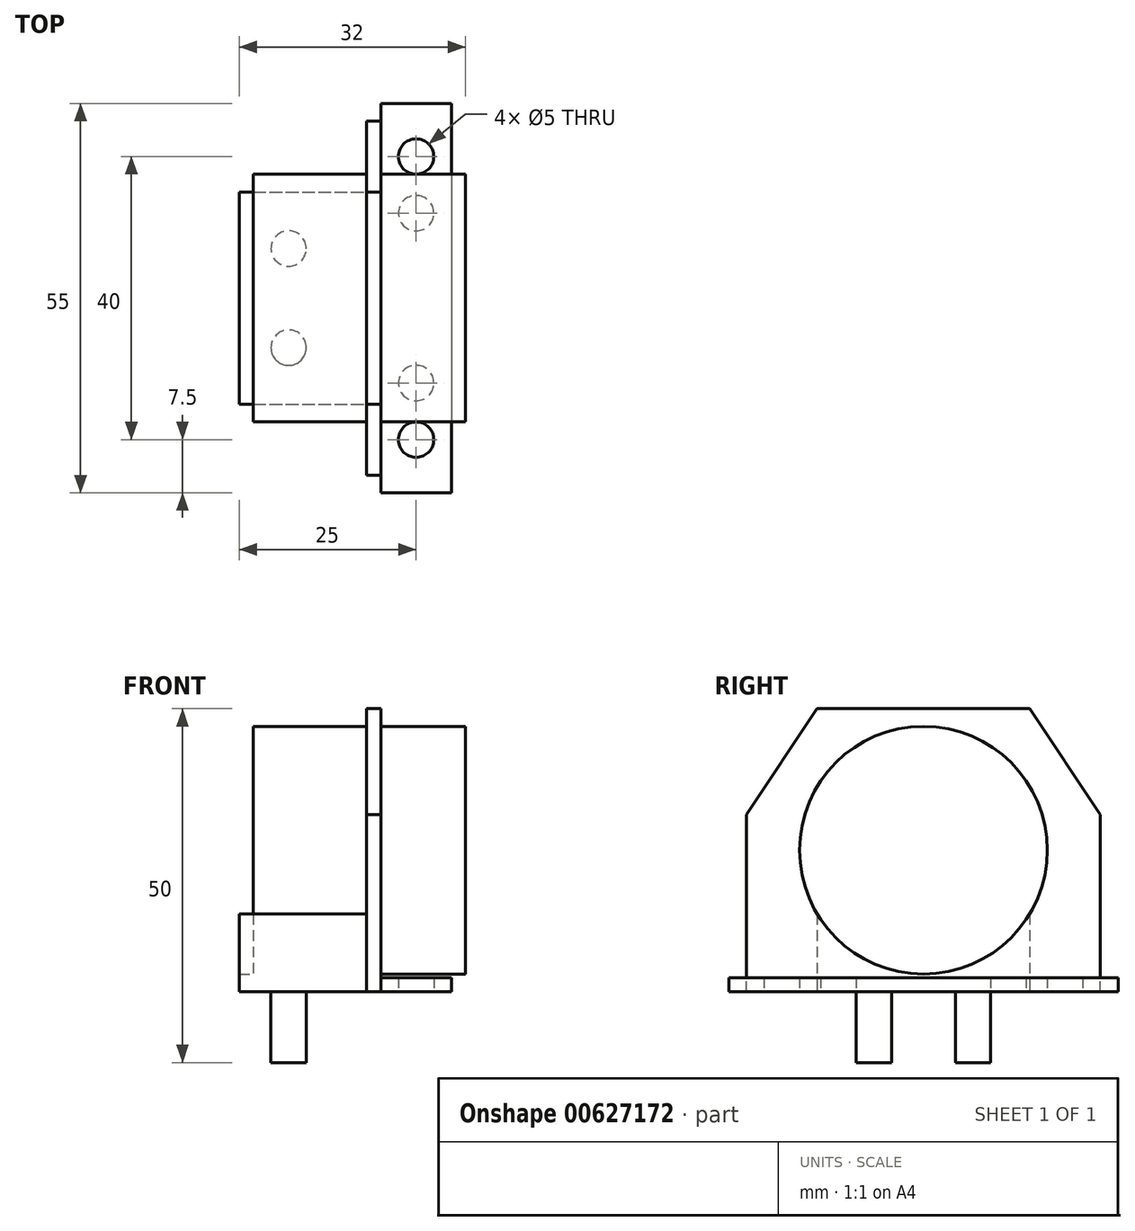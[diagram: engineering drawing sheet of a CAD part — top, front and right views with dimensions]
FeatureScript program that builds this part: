
annotation { "Feature Type Name" : "Feature", "Feature Type Description" : "" }
export const myFeature = defineFeature(function(context is Context, id is Id, definition is map)
    precondition{}
    {
        {
            var Q0;
            Q0=qCreatedBy(makeId("Top.planeOp"),FACE);
            var sketch = newSketch(context, id + "F0", { "sketchPlane" : qUnion([Q0])});
            skLineSegment(sketch, "E0.bottom", {"start": v(5, 27.5) * mm, "end": v(-5, 27.5) * mm});
            skLineSegment(sketch, "E0.top", {"start": v(5, -27.5) * mm, "end": v(-5, -27.5) * mm});
            skLineSegment(sketch, "E0.left", {"start": v(5, 27.5) * mm, "end": v(5, -27.5) * mm});
            skLineSegment(sketch, "E0.right", {"start": v(-5, 27.5) * mm, "end": v(-5, -27.5) * mm});
            skPoint(sketch, "E0.middle", {"position": v(0, 0) * mm});
            skCircle(sketch, "E1", {"center": v(0, 20) * mm, "radius": 2.5 * mm});
            skCircle(sketch, "E2", {"center": v(0, 12) * mm, "radius": 2.5 * mm});
            skCircle(sketch, "E3.MirrorC", {"center": v(0, -12) * mm, "radius": 2.5 * mm});
            skCircle(sketch, "E4.MirrorC", {"center": v(0, -20) * mm, "radius": 2.5 * mm});
            skSolve(sketch);
        }
        {
            var Q0;
            Q0 = qSketchRegion(id + "F0", true);
            extrude(context, id + "F1", {"entities" : qUnion([Q0]), "depth" : 2 * mm, "offsetDistance" : 25 * mm});
        }
        {
            var Q0;
            Q0=makeQuery(id+"F1.opExtrude","SWEPT_FACE",FACE,{"disambiguationData":[OSD([sQuery(id+"F0.wireOp",EDGE,"E0.right")])]});
            var sketch = newSketch(context, id + "F2", { "sketchPlane" : qUnion([Q0])});
            skLineSegment(sketch, "E5", {"start": v(-25, 0) * mm, "end": v(-25, 25) * mm});
            skLineSegment(sketch, "E6", {"start": v(-15, 0) * mm, "end": v(-15, 40) * mm});
            skLineSegment(sketch, "E7", {"start": v(-25, 25) * mm, "end": v(-15, 40) * mm});
            skLineSegment(sketch, "E8", {"start": v(0, 40) * mm, "end": v(-15, 40) * mm});
            skLineSegment(sketch, "E9.MirrorCS", {"start": v(0, 40) * mm, "end": v(15, 40) * mm});
            skLineSegment(sketch, "E10.MirrorCS", {"start": v(15, 0) * mm, "end": v(15, 40) * mm});
            skLineSegment(sketch, "E11.MirrorCS", {"start": v(25, 25) * mm, "end": v(15, 40) * mm});
            skLineSegment(sketch, "E12.MirrorCS", {"start": v(25, 0) * mm, "end": v(25, 25) * mm});
            skCircle(sketch, "E13", {"center": v(0, 20) * mm, "radius": 17.5 * mm});
            skSolve(sketch);
        }
        {
            var Q0;
            {var subQ0=sQuery(id+"F2.wireOp",EDGE,"E6");var subQ1=sQuery(id+"F0.wireOp",EDGE,"E0.right");var subQ2=makeQuery(id+"F1.opExtrude","CAP_EDGE",EDGE,{"disambiguationData":[OSD([subQ1])],"isStart":true});var subQ3=makeQuery(id+"F2.imprint","INTERSECT",VERTEX,{"derivedFrom":[subQ2,subQ0]});Q0=makeQuery(id+"F2.imprint","IMPRINT",FACE,{"disambiguationData":[TD([[makeQuery(id+"F2.imprint","IMPRINT",EDGE,{"disambiguationData":[TD([[subQ3,-1.0]])],"derivedFrom":subQ0}),-1.0]])]});}
            var Q1;
            {var subQ0=sQuery(id+"F2.wireOp",EDGE,"E5");var subQ1=sQuery(id+"F0.wireOp",EDGE,"E0.right");var subQ2=makeQuery(id+"F1.opExtrude","CAP_EDGE",EDGE,{"disambiguationData":[OSD([subQ1])],"isStart":true});var subQ3=makeQuery(id+"F2.imprint","INTERSECT",VERTEX,{"derivedFrom":[subQ2,subQ0]});Q1=makeQuery(id+"F2.imprint","IMPRINT",FACE,{"disambiguationData":[TD([[makeQuery(id+"F2.imprint","IMPRINT",EDGE,{"disambiguationData":[TD([[subQ3,-1.0]])],"derivedFrom":subQ0}),-1.0]])]});}
            var Q2;
            {var subQ0=sQuery(id+"F2.wireOp",EDGE,"E10.MirrorCS");var subQ1=sQuery(id+"F0.wireOp",EDGE,"E0.right");var subQ2=makeQuery(id+"F1.opExtrude","CAP_EDGE",EDGE,{"disambiguationData":[OSD([subQ1])],"isStart":true});var subQ3=makeQuery(id+"F2.imprint","INTERSECT",VERTEX,{"derivedFrom":[subQ2,subQ0]});Q2=makeQuery(id+"F2.imprint","IMPRINT",FACE,{"disambiguationData":[TD([[makeQuery(id+"F2.imprint","IMPRINT",EDGE,{"disambiguationData":[TD([[subQ3,-1.0]])],"derivedFrom":subQ0}),-1.0]])]});}
            var Q3;
            {var subQ0=sQuery(id+"F2.wireOp",EDGE,"E7");Q3=makeQuery(id+"F2.imprint","IMPRINT",FACE,{"disambiguationData":[TD([[makeQuery(id+"F2.imprint","IMPRINT",EDGE,{"derivedFrom":subQ0}),-1.0]])]});}
            var Q4;
            {var subQ0=sQuery(id+"F2.wireOp",EDGE,"E13");var subQ1=sQuery(id+"F2.wireOp",EDGE,"E6");var subQ2=makeQuery(id+"F2.imprint","INTERSECT",VERTEX,{"disambiguationData":[OD(0.0)],"derivedFrom":[subQ1,subQ0]});Q4=makeQuery(id+"F2.imprint","IMPRINT",FACE,{"disambiguationData":[TD([[makeQuery(id+"F2.imprint","IMPRINT",EDGE,{"disambiguationData":[TD([[subQ2,1.0]])],"derivedFrom":subQ1}),-1.0]])]});}
            var Q5;
            {var subQ0=sQuery(id+"F2.wireOp",EDGE,"E11.MirrorCS");Q5=makeQuery(id+"F2.imprint","IMPRINT",FACE,{"disambiguationData":[TD([[makeQuery(id+"F2.imprint","IMPRINT",EDGE,{"derivedFrom":subQ0}),1.0]])]});}
            var Q6;
            {var subQ4=sQuery(id+"F2.wireOp",EDGE,"E8");Q6=makeQuery(id+"F2.imprint","IMPRINT",FACE,{"disambiguationData":[TD([[makeQuery(id+"F2.imprint","IMPRINT",EDGE,{"derivedFrom":subQ4}),1.0]])]});}
            extrude(context, id + "F3", {"entities" : qUnion([Q0, Q1, Q2, Q3, Q4, Q5, Q6]), "operationType" : NewBodyOperationType.ADD, "depth" : 2 * mm, "offsetDistance" : 25 * mm});
        }
        {
            var Q0;
            {var subQ0=sQuery(id+"F2.wireOp",EDGE,"E13");var subQ1=sQuery(id+"F2.wireOp",EDGE,"E6");var subQ2=makeQuery(id+"F2.imprint","INTERSECT",VERTEX,{"disambiguationData":[OD(0.0)],"derivedFrom":[subQ1,subQ0]});Q0=makeQuery(id+"F2.imprint","IMPRINT",FACE,{"disambiguationData":[TD([[makeQuery(id+"F2.imprint","IMPRINT",EDGE,{"disambiguationData":[TD([[subQ2,-1.0]])],"derivedFrom":subQ1}),-1.0]])]});}
            var Q1;
            {var subQ0=sQuery(id+"F2.wireOp",EDGE,"E13");var subQ1=sQuery(id+"F2.wireOp",EDGE,"E10.MirrorCS");var subQ2=makeQuery(id+"F2.imprint","INTERSECT",VERTEX,{"disambiguationData":[OD(0.0)],"derivedFrom":[subQ1,subQ0]});Q1=makeQuery(id+"F2.imprint","IMPRINT",FACE,{"disambiguationData":[TD([[makeQuery(id+"F2.imprint","IMPRINT",EDGE,{"disambiguationData":[TD([[subQ2,-1.0]])],"derivedFrom":subQ1}),-1.0]])]});}
            var Q2;
            {var subQ0=sQuery(id+"F2.wireOp",EDGE,"E13");var subQ1=sQuery(id+"F2.wireOp",EDGE,"E6");var subQ2=makeQuery(id+"F2.imprint","INTERSECT",VERTEX,{"disambiguationData":[OD(0.0)],"derivedFrom":[subQ1,subQ0]});Q2=makeQuery(id+"F2.imprint","IMPRINT",FACE,{"disambiguationData":[TD([[makeQuery(id+"F2.imprint","IMPRINT",EDGE,{"disambiguationData":[TD([[subQ2,-1.0]])],"derivedFrom":subQ1}),1.0]])]});}
            extrude(context, id + "F4", {"entities" : qUnion([Q0, Q1, Q2]), "operationType" : NewBodyOperationType.ADD, "oppositeDirection" : true, "depth" : 12 * mm, "offsetDistance" : 25 * mm, "hasSecondDirection" : true, "secondDirectionOppositeDirection" : false, "secondDirectionDepth" : 18 * mm});
        }
        {
            var Q0;
            {var subQ0=sQuery(id+"F2.wireOp",EDGE,"E13");var subQ1=sQuery(id+"F2.wireOp",EDGE,"E6");var subQ2=makeQuery(id+"F2.imprint","INTERSECT",VERTEX,{"disambiguationData":[OD(0.0)],"derivedFrom":[subQ1,subQ0]});Q0=makeQuery(id+"F2.imprint","IMPRINT",FACE,{"disambiguationData":[TD([[makeQuery(id+"F2.imprint","IMPRINT",EDGE,{"disambiguationData":[TD([[subQ2,1.0]])],"derivedFrom":subQ1}),-1.0]])]});}
            var Q1;
            {var subQ0=sQuery(id+"F2.wireOp",EDGE,"E6");var subQ1=sQuery(id+"F0.wireOp",EDGE,"E0.right");var subQ2=makeQuery(id+"F1.opExtrude","CAP_EDGE",EDGE,{"disambiguationData":[OSD([subQ1])],"isStart":true});var subQ3=makeQuery(id+"F2.imprint","INTERSECT",VERTEX,{"derivedFrom":[subQ2,subQ0]});Q1=makeQuery(id+"F2.imprint","IMPRINT",FACE,{"disambiguationData":[TD([[makeQuery(id+"F2.imprint","IMPRINT",EDGE,{"disambiguationData":[TD([[subQ3,-1.0]])],"derivedFrom":subQ0}),-1.0]])]});}
            extrude(context, id + "F5", {"entities" : qUnion([Q0, Q1]), "operationType" : NewBodyOperationType.ADD, "depth" : 20 * mm, "offsetDistance" : 25 * mm});
        }
        {
            var Q0;
            {var subQ0=sQuery(id+"F0.wireOp",EDGE,"E0.right");Q0=makeQuery(id+"F5.boolean.opBoolean","MERGE",FACE,{"derivedFrom":[makeQuery(id+"F3.boolean.opBoolean","MERGE",FACE,{"derivedFrom":[makeQuery(id+"F1.opExtrude","CAP_FACE",FACE,{"disambiguationData":[OSD([sQuery(id+"F0.wireOp",EDGE,"E0.bottom"),sQuery(id+"F0.wireOp",EDGE,"E0.top"),sQuery(id+"F0.wireOp",EDGE,"E0.left"),subQ0,sQuery(id+"F0.wireOp",EDGE,"E1"),sQuery(id+"F0.wireOp",EDGE,"E2"),sQuery(id+"F0.wireOp",EDGE,"E3.MirrorC"),sQuery(id+"F0.wireOp",EDGE,"E4.MirrorC")])],"isStart":true}),makeQuery(id+"F3.opExtrude","SWEPT_FACE",FACE,{"disambiguationData":[OSD([subQ0])]})]}),makeQuery(id+"F5.opExtrude","SWEPT_FACE",FACE,{"disambiguationData":[OSD([subQ0])]})]});}
            var sketch = newSketch(context, id + "F6", { "sketchPlane" : qUnion([Q0])});
            skCircle(sketch, "E14", {"center": v(-18, -7) * mm, "radius": 2.5 * mm});
            skCircle(sketch, "E15.MirrorC", {"center": v(-18, 7) * mm, "radius": 2.5 * mm});
            skSolve(sketch);
        }
        {
            var Q0;
            Q0 = qSketchRegion(id + "F6", true);
            extrude(context, id + "F7", {"entities" : qUnion([Q0]), "operationType" : NewBodyOperationType.ADD, "depth" : 10 * mm, "offsetDistance" : 25 * mm});
        }
    });
